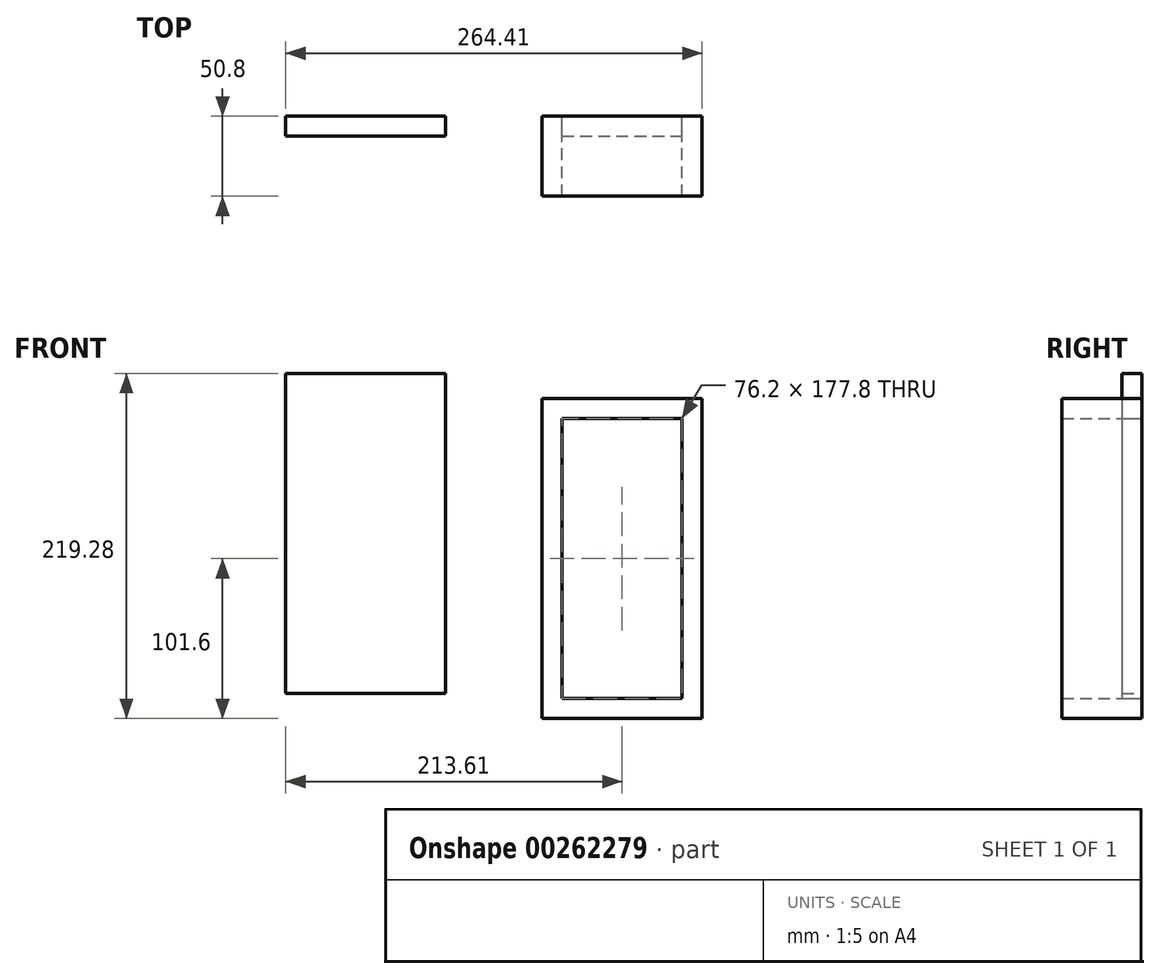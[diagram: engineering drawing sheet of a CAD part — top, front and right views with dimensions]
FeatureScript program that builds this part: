
annotation { "Feature Type Name" : "Feature", "Feature Type Description" : "" }
export const myFeature = defineFeature(function(context is Context, id is Id, definition is map)
    precondition{}
    {
        {
            var Q0;
            Q0=qCreatedBy(makeId("Front.planeOp"),FACE);
            var sketch = newSketch(context, id + "F0", { "sketchPlane" : qUnion([Q0])});
            skLineSegment(sketch, "E0.bottom", {"start": v(50.8, 101.6) * mm, "end": v(-50.8, 101.6) * mm});
            skLineSegment(sketch, "E0.top", {"start": v(50.8, -101.6) * mm, "end": v(-50.8, -101.6) * mm});
            skLineSegment(sketch, "E0.left", {"start": v(50.8, 101.6) * mm, "end": v(50.8, -101.6) * mm});
            skLineSegment(sketch, "E0.right", {"start": v(-50.8, 101.6) * mm, "end": v(-50.8, -101.6) * mm});
            skPoint(sketch, "E0.middle", {"position": v(0, 0) * mm});
            skLineSegment(sketch, "E1.bottom", {"start": v(-38.1, 88.9) * mm, "end": v(38.1, 88.9) * mm});
            skLineSegment(sketch, "E1.top", {"start": v(-38.1, -88.9) * mm, "end": v(38.1, -88.9) * mm});
            skLineSegment(sketch, "E1.left", {"start": v(-38.1, 88.9) * mm, "end": v(-38.1, -88.9) * mm});
            skLineSegment(sketch, "E1.right", {"start": v(38.1, 88.9) * mm, "end": v(38.1, -88.9) * mm});
            skLineSegment(sketch, "E2.bottom", {"start": v(-112, 117.68) * mm, "end": v(-213.6, 117.68) * mm});
            skLineSegment(sketch, "E2.top", {"start": v(-112, -85.52) * mm, "end": v(-213.6, -85.52) * mm});
            skLineSegment(sketch, "E2.left", {"start": v(-112, 117.68) * mm, "end": v(-112, -85.52) * mm});
            skLineSegment(sketch, "E2.right", {"start": v(-213.6, 117.68) * mm, "end": v(-213.6, -85.52) * mm});
            skPoint(sketch, "E2.middle", {"position": v(-162.8, 16.08) * mm});
            skSolve(sketch);
        }
        {
            var Q0;
            Q0=makeQuery(id+"F0.imprint","IMPRINT",FACE,{"disambiguationData":[TD([[makeQuery(id+"F0.imprint","IMPRINT",EDGE,{"derivedFrom":sQuery(id+"F0.wireOp",EDGE,"E0.bottom")}),1.0]])]});
            extrude(context, id + "F1", {"entities" : qUnion([Q0]), "depth" : 50.8 * mm});
        }
        {
            var Q0;
            Q0=makeQuery(id+"F0.imprint","IMPRINT",FACE,{"disambiguationData":[TD([[makeQuery(id+"F0.imprint","IMPRINT",EDGE,{"derivedFrom":sQuery(id+"F0.wireOp",EDGE,"E1.bottom")}),-1.0]])]});
            extrude(context, id + "F2", {"entities" : qUnion([Q0]), "depth" : 12.7 * mm});
        }
        {
            var Q0;
            Q0=makeQuery(id+"F0.imprint","IMPRINT",FACE,{"disambiguationData":[TD([[makeQuery(id+"F0.imprint","IMPRINT",EDGE,{"derivedFrom":sQuery(id+"F0.wireOp",EDGE,"E2.bottom")}),1.0]])]});
            extrude(context, id + "F3", {"entities" : qUnion([Q0]), "depth" : 12.7 * mm});
        }
    });
